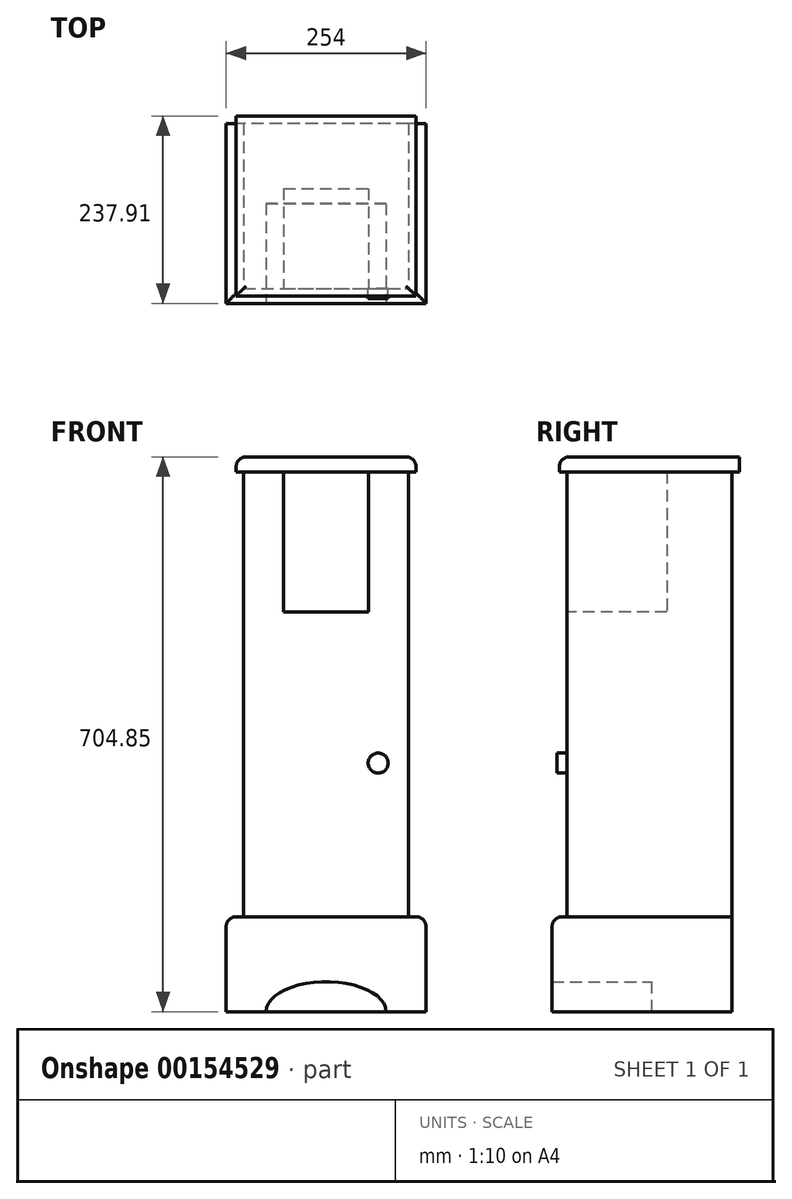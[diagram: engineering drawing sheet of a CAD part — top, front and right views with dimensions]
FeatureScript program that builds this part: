
annotation { "Feature Type Name" : "Feature", "Feature Type Description" : "" }
export const myFeature = defineFeature(function(context is Context, id is Id, definition is map)
    precondition{}
    {
        {
            var Q0;
            Q0=qCreatedBy(makeId("Top.planeOp"),FACE);
            var sketch = newSketch(context, id + "F0", { "sketchPlane" : qUnion([Q0])});
            skLineSegment(sketch, "E0.bottom", {"start": v(127, 114.3) * mm, "end": v(-127, 114.3) * mm});
            skLineSegment(sketch, "E0.top", {"start": v(127, -114.3) * mm, "end": v(-127, -114.3) * mm});
            skLineSegment(sketch, "E0.left", {"start": v(127, 114.3) * mm, "end": v(127, -114.3) * mm});
            skLineSegment(sketch, "E0.right", {"start": v(-127, 114.3) * mm, "end": v(-127, -114.3) * mm});
            skPoint(sketch, "E0.middle", {"position": v(0, 0) * mm});
            skSolve(sketch);
        }
        {
            var Q0;
            Q0=makeQuery(id+"F0.imprint","IMPRINT",FACE,{"disambiguationData":[TD([[makeQuery(id+"F0.imprint","IMPRINT",EDGE,{"derivedFrom":sQuery(id+"F0.wireOp",EDGE,"E0.bottom")}),1.0]])]});
            extrude(context, id + "F1", {"entities" : qUnion([Q0]), "depth" : 120.65 * mm});
        }
        {
            var Q0;
            Q0=makeQuery(id+"F1.opExtrude","CAP_FACE",FACE,{"disambiguationData":[OSD([sQuery(id+"F0.wireOp",EDGE,"E0.bottom"),sQuery(id+"F0.wireOp",EDGE,"E0.top"),sQuery(id+"F0.wireOp",EDGE,"E0.left"),sQuery(id+"F0.wireOp",EDGE,"E0.right")])],"isStart":false});
            var sketch = newSketch(context, id + "F2", { "sketchPlane" : qUnion([Q0])});
            skLineSegment(sketch, "E1.bottom", {"start": v(-104.78, 114.3) * mm, "end": v(104.78, 114.3) * mm});
            skLineSegment(sketch, "E1.top", {"start": v(-104.78, -95.25) * mm, "end": v(104.78, -95.25) * mm});
            skLineSegment(sketch, "E1.left", {"start": v(-104.78, 114.3) * mm, "end": v(-104.78, -95.25) * mm});
            skLineSegment(sketch, "E1.right", {"start": v(104.78, 114.3) * mm, "end": v(104.78, -95.25) * mm});
            skLineSegment(sketch, "E2", {"start": v(-104.78, 9.53) * mm, "end": v(-127, 9.53) * mm, "construction": true});
            skLineSegment(sketch, "E3", {"start": v(104.78, 9.53) * mm, "end": v(127, 9.53) * mm, "construction": true});
            skSolve(sketch);
        }
        {
            var Q0;
            Q0=makeQuery(id+"F2.imprint","IMPRINT",FACE,{"disambiguationData":[TD([[makeQuery(id+"F2.imprint","IMPRINT",EDGE,{"derivedFrom":sQuery(id+"F2.wireOp",EDGE,"E1.bottom")}),1.0]])]});
            extrude(context, id + "F3", {"entities" : qUnion([Q0]), "operationType" : NewBodyOperationType.ADD, "depth" : 565.15 * mm});
        }
        {
            var Q0;
            Q0=makeQuery(id+"F3.opExtrude","CAP_FACE",FACE,{"disambiguationData":[OSD([sQuery(id+"F2.wireOp",EDGE,"E1.bottom"),sQuery(id+"F2.wireOp",EDGE,"E1.top"),sQuery(id+"F2.wireOp",EDGE,"E1.left"),sQuery(id+"F2.wireOp",EDGE,"E1.right")])],"isStart":false});
            var sketch = newSketch(context, id + "F4", { "sketchPlane" : qUnion([Q0])});
            skLineSegment(sketch, "E4.bottom", {"start": v(-114.3, 123.6) * mm, "end": v(114.3, 123.6) * mm});
            skLineSegment(sketch, "E4.top", {"start": v(-114.3, -105) * mm, "end": v(114.3, -105) * mm});
            skLineSegment(sketch, "E4.left", {"start": v(-114.3, 123.6) * mm, "end": v(-114.3, -105) * mm});
            skLineSegment(sketch, "E4.right", {"start": v(114.3, 123.6) * mm, "end": v(114.3, -105) * mm});
            skLineSegment(sketch, "E5", {"start": v(0, -105) * mm, "end": v(0, -95.25) * mm});
            skLineSegment(sketch, "E6", {"start": v(-114.3, 9.3) * mm, "end": v(-104.78, 9.3) * mm, "construction": true});
            skPoint(sketch, "E6.endSnap0", {"position": v(-104.78, 9.53) * mm});
            skSolve(sketch);
        }
        {
            var Q0;
            Q0=makeQuery(id+"F4.imprint","IMPRINT",FACE,{"disambiguationData":[TD([[makeQuery(id+"F4.imprint","IMPRINT",EDGE,{"derivedFrom":sQuery(id+"F4.wireOp",EDGE,"E4.bottom")}),-1.0]])]});
            var Q1;
            Q1=makeQuery(id+"F4.imprint","IMPRINT",FACE,{"disambiguationData":[TD([[makeQuery(id+"F4.imprint","IMPRINT",EDGE,{"derivedFrom":makeQuery(id+"F3.opExtrude","CAP_EDGE",EDGE,{"disambiguationData":[OSD([sQuery(id+"F2.wireOp",EDGE,"E1.bottom")])],"isStart":false})}),1.0]])]});
            extrude(context, id + "F5", {"entities" : qUnion([Q0, Q1]), "operationType" : NewBodyOperationType.ADD, "depth" : 19.05 * mm});
        }
        {
            var Q0;
            Q0=makeQuery(id+"F3.opExtrude","SWEPT_FACE",FACE,{"disambiguationData":[OSD([sQuery(id+"F2.wireOp",EDGE,"E1.top")])]});
            var sketch = newSketch(context, id + "F6", { "sketchPlane" : qUnion([Q0])});
            skLineSegment(sketch, "E7.bottom", {"start": v(-53.98, 685.8) * mm, "end": v(53.98, 685.8) * mm});
            skLineSegment(sketch, "E7.top", {"start": v(-53.98, 508) * mm, "end": v(53.98, 508) * mm});
            skLineSegment(sketch, "E7.left", {"start": v(-53.98, 685.8) * mm, "end": v(-53.98, 508) * mm});
            skLineSegment(sketch, "E7.right", {"start": v(53.98, 685.8) * mm, "end": v(53.98, 508) * mm});
            skLineSegment(sketch, "E8", {"start": v(0, 508) * mm, "end": v(0, 120.65) * mm, "construction": true});
            skPoint(sketch, "E8.startSnap0", {"position": v(0, 508) * mm});
            skSolve(sketch);
        }
        {
            var Q0;
            Q0=makeQuery(id+"F6.imprint","IMPRINT",FACE,{"disambiguationData":[TD([[makeQuery(id+"F6.imprint","IMPRINT",EDGE,{"derivedFrom":sQuery(id+"F6.wireOp",EDGE,"E7.bottom")}),-1.0]])]});
            extrude(context, id + "F7", {"entities" : qUnion([Q0]), "operationType" : NewBodyOperationType.REMOVE, "oppositeDirection" : true, "depth" : 127 * mm});
        }
        {
            var Q0;
            Q0=makeQuery(id+"F3.opExtrude","SWEPT_FACE",FACE,{"disambiguationData":[OSD([sQuery(id+"F2.wireOp",EDGE,"E1.top")])]});
            var sketch = newSketch(context, id + "F8", { "sketchPlane" : qUnion([Q0])});
            skCircle(sketch, "E9", {"center": v(66.19, 315.89) * mm, "radius": 12.7 * mm});
            skSolve(sketch);
        }
        {
            var Q0;
            Q0=makeQuery(id+"F8.imprint","IMPRINT",FACE,{"disambiguationData":[TD([[makeQuery(id+"F8.imprint","IMPRINT",EDGE,{"derivedFrom":sQuery(id+"F8.wireOp",EDGE,"E9")}),1.0]])]});
            extrude(context, id + "F9", {"entities" : qUnion([Q0]), "operationType" : NewBodyOperationType.ADD, "depth" : 12.7 * mm});
        }
        {
            var Q0;
            Q0=makeQuery(id+"F1.opExtrude","CAP_EDGE",EDGE,{"disambiguationData":[OSD([sQuery(id+"F0.wireOp",EDGE,"E0.left")])],"isStart":false});
            var Q1;
            Q1=makeQuery(id+"F1.opExtrude","CAP_EDGE",EDGE,{"disambiguationData":[OSD([sQuery(id+"F0.wireOp",EDGE,"E0.top")])],"isStart":false});
            var Q2;
            Q2=makeQuery(id+"F1.opExtrude","CAP_EDGE",EDGE,{"disambiguationData":[OSD([sQuery(id+"F0.wireOp",EDGE,"E0.right")])],"isStart":false});
            var Q3;
            Q3=makeQuery(id+"F5.opExtrude","CAP_EDGE",EDGE,{"disambiguationData":[OSD([sQuery(id+"F4.wireOp",EDGE,"E4.right")])],"isStart":false});
            var Q4;
            Q4=makeQuery(id+"F5.opExtrude","CAP_EDGE",EDGE,{"disambiguationData":[OSD([sQuery(id+"F4.wireOp",EDGE,"E4.top")])],"isStart":false});
            var Q5;
            Q5=makeQuery(id+"F5.opExtrude","CAP_EDGE",EDGE,{"disambiguationData":[OSD([sQuery(id+"F4.wireOp",EDGE,"E4.left")])],"isStart":false});
            fillet(context, id + "F10", {"entities" : qUnion([Q0, Q1, Q2, Q3, Q4, Q5]), "radius" : 12.7 * mm, "tangentPropagation" : true, "allowEdgeOverflow" : false});
        }
        {
            var Q0;
            Q0=makeQuery(id+"F1.opExtrude","SWEPT_FACE",FACE,{"disambiguationData":[OSD([sQuery(id+"F0.wireOp",EDGE,"E0.top")])]});
            var sketch = newSketch(context, id + "F11", { "sketchPlane" : qUnion([Q0])});
            skEllipse(sketch, "E10", {"center": v(0, 0) * mm, "majorRadius": 76.2 * mm, "minorRadius": 38.1 * mm, "majorAxis": v(1, 0)});
            skSolve(sketch);
        }
        {
            var Q0;
            {var subQ0=sQuery(id+"F11.wireOp",EDGE,"E10");var subQ1=makeQuery(id+"F1.opExtrude","CAP_EDGE",EDGE,{"disambiguationData":[OSD([sQuery(id+"F0.wireOp",EDGE,"E0.top")])],"isStart":true});var subQ2=makeQuery(id+"F11.imprint","INTERSECT",VERTEX,{"disambiguationData":[OD(0.0)],"derivedFrom":[subQ1,subQ0]});Q0=makeQuery(id+"F11.imprint","IMPRINT",FACE,{"disambiguationData":[TD([[makeQuery(id+"F11.imprint","IMPRINT",EDGE,{"disambiguationData":[TD([[subQ2,1.0]])],"derivedFrom":subQ0}),1.0]])]});}
            var Q1;
            {var subQ0=sQuery(id+"F11.wireOp",EDGE,"E10");var subQ1=makeQuery(id+"F1.opExtrude","CAP_EDGE",EDGE,{"disambiguationData":[OSD([sQuery(id+"F0.wireOp",EDGE,"E0.top")])],"isStart":true});var subQ2=makeQuery(id+"F11.imprint","INTERSECT",VERTEX,{"disambiguationData":[OD(0.0)],"derivedFrom":[subQ1,subQ0]});Q1=makeQuery(id+"F11.imprint","IMPRINT",FACE,{"disambiguationData":[TD([[makeQuery(id+"F11.imprint","IMPRINT",EDGE,{"disambiguationData":[TD([[subQ2,-1.0]])],"derivedFrom":subQ0}),1.0]])]});}
            extrude(context, id + "F12", {"entities" : qUnion([Q0, Q1]), "operationType" : NewBodyOperationType.REMOVE, "oppositeDirection" : true, "depth" : 127 * mm});
        }
    });
